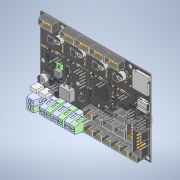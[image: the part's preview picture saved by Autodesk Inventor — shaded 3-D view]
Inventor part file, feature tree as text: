
AUTODESK INVENTOR PART (.ipt)
format: ipt  version: 2022 (Build 260153000, 153)  size: 26,488,320 bytes
history: native  units: in
note: dims shown in document units (in); Inventor stores cm internally (conversion verified against a paired STEP export)
features: other x489, extrude x194, sketch x22, fillet x4
ambient origin geometry x8: Origin, YZ Plane, XZ Plane, XY Plane, X Axis, Y Axis, Z Axis, Center Point
bodies: Solid1 (feature_tree), Solid2 (feature_tree), Solid3 (feature_tree), Solid4 (feature_tree), Solid5 (feature_tree), Solid6 (feature_tree), Solid7 (feature_tree), Solid8 (feature_tree), Solid9 (feature_tree), Solid10 (feature_tree), Solid11 (feature_tree), Solid12 (feature_tree), Solid13 (feature_tree), Solid14 (feature_tree), Solid15 (feature_tree), Solid16 (feature_tree), Solid17 (feature_tree), Solid18 (feature_tree), Solid19 (feature_tree), Solid20 (feature_tree), Solid21 (feature_tree), Solid22 (feature_tree), Solid23 (feature_tree), Solid24 (feature_tree), Solid25 (feature_tree), Solid26 (feature_tree), Solid27 (feature_tree), Solid28 (feature_tree), Solid29 (feature_tree), Solid30 (feature_tree), Solid31 (feature_tree), Solid32 (feature_tree), Solid33 (feature_tree), Solid34 (feature_tree), Solid35 (feature_tree), Solid36 (feature_tree), Solid37 (feature_tree), Solid38 (feature_tree), Solid39 (feature_tree), Solid40 (feature_tree), Solid41 (feature_tree), Solid42 (feature_tree), Solid43 (feature_tree), Solid44 (feature_tree), Solid45 (feature_tree), Solid46 (feature_tree), Solid47 (feature_tree), Solid48 (feature_tree), Solid49 (feature_tree), Solid50 (feature_tree), Solid51 (feature_tree), Solid52 (feature_tree), Solid53 (feature_tree), Solid54 (feature_tree), Solid55 (feature_tree), Solid56 (feature_tree), Solid57 (feature_tree), Solid58 (feature_tree), Solid59 (feature_tree), Solid60 (feature_tree), Solid61 (feature_tree), Solid62 (feature_tree), Solid63 (feature_tree), Solid64 (feature_tree), Solid65 (feature_tree), Solid66 (feature_tree), Solid67 (feature_tree), Solid68 (feature_tree), Solid69 (feature_tree), Solid70 (feature_tree), Solid71 (feature_tree), Solid72 (feature_tree), Solid73 (feature_tree), Solid74 (feature_tree), Solid75 (feature_tree), Solid76 (feature_tree), Solid77 (feature_tree), Solid78 (feature_tree), Solid79 (feature_tree), Solid80 (feature_tree), Solid81 (feature_tree), Solid82 (feature_tree), Solid83 (feature_tree), Solid84 (feature_tree), Solid85 (feature_tree), Solid86 (feature_tree), Solid87 (feature_tree), Solid88 (feature_tree), Solid89 (feature_tree), Solid90 (feature_tree), Solid91 (feature_tree), Solid92 (feature_tree), Solid93 (feature_tree), Solid94 (feature_tree), Solid95 (feature_tree), Solid96 (feature_tree), Solid97 (feature_tree), Solid98 (feature_tree), Solid99 (feature_tree), Solid100 (feature_tree), Solid101 (feature_tree), Solid102 (feature_tree), Solid103 (feature_tree), Solid104 (feature_tree), Solid105 (feature_tree), Solid106 (feature_tree), Solid107 (feature_tree), Solid108 (feature_tree), Solid109 (feature_tree), Solid110 (feature_tree), Solid111 (feature_tree), Solid112 (feature_tree), Solid113 (feature_tree), Solid114 (feature_tree), Solid115 (feature_tree), Solid116 (feature_tree), Solid117 (feature_tree), Solid118 (feature_tree), Solid119 (feature_tree), Solid120 (feature_tree), Solid121 (feature_tree), Solid122 (feature_tree), Solid123 (feature_tree), Solid124 (feature_tree), Solid125 (feature_tree), Solid126 (feature_tree), Solid127 (feature_tree), Solid128 (feature_tree), Solid129 (feature_tree), Solid130 (feature_tree), Solid131 (feature_tree), Solid132 (feature_tree), Solid133 (feature_tree), Solid134 (feature_tree), Solid135 (feature_tree), Solid136 (feature_tree), Solid137 (feature_tree), Solid138 (feature_tree), Solid139 (feature_tree), Solid140 (feature_tree), Solid141 (feature_tree), Solid142 (feature_tree), Solid143 (feature_tree), Solid144 (feature_tree), Solid145 (feature_tree), Solid146 (feature_tree), Solid147 (feature_tree), Solid148 (feature_tree), Solid149 (feature_tree), Solid150 (feature_tree), Solid151 (feature_tree), Solid152 (feature_tree), Solid153 (feature_tree), Solid154 (feature_tree), Solid155 (feature_tree), Solid156 (feature_tree), Solid157 (feature_tree), Solid158 (feature_tree), Solid159 (feature_tree), Solid160 (feature_tree), Solid161 (feature_tree), Solid162 (feature_tree), Solid163 (feature_tree), Solid164 (feature_tree), Solid165 (feature_tree), Solid166 (feature_tree), Solid167 (feature_tree), Solid168 (feature_tree), Solid169 (feature_tree), Solid170 (feature_tree), Solid171 (feature_tree), Solid172 (feature_tree), Solid173 (feature_tree), Solid174 (feature_tree), Solid175 (feature_tree), Solid176 (feature_tree), Solid177 (feature_tree), Solid178 (feature_tree), Solid179 (feature_tree), Solid180 (feature_tree), Solid181 (feature_tree), Solid182 (feature_tree), Solid183 (feature_tree), Solid184 (feature_tree), Solid185 (feature_tree), Solid186 (feature_tree), Solid187 (feature_tree), Solid188 (feature_tree), Solid189 (feature_tree), Solid190 (feature_tree), Solid191 (feature_tree), Solid192 (feature_tree), Solid193 (feature_tree), Solid194 (feature_tree), Solid195 (feature_tree), Solid196 (feature_tree), Solid197 (feature_tree), Solid198 (feature_tree), Solid199 (feature_tree), Solid200 (feature_tree), Solid201 (feature_tree), Solid202 (feature_tree), Solid203 (feature_tree), Solid204 (feature_tree), Solid205 (feature_tree), Solid206 (feature_tree), Solid207 (feature_tree), Solid208 (feature_tree), Solid209 (feature_tree), Solid210 (feature_tree), Solid211 (feature_tree), Solid212 (feature_tree), Solid213 (feature_tree), Solid214 (feature_tree), Solid215 (feature_tree), Solid216 (feature_tree), Solid217 (feature_tree), Solid218 (feature_tree), Solid219 (feature_tree), Solid220 (feature_tree), Solid221 (feature_tree), Solid222 (feature_tree), Solid223 (feature_tree), Solid224 (feature_tree), Solid225 (feature_tree), Solid226 (feature_tree), Solid227 (feature_tree), Solid228 (feature_tree), Solid229 (feature_tree), Solid230 (feature_tree), Solid231 (feature_tree), Solid232 (feature_tree), Solid233 (feature_tree), Solid234 (feature_tree), Solid235 (feature_tree), Solid236 (feature_tree), Solid237 (feature_tree), Solid238 (feature_tree), Solid239 (feature_tree), Solid240 (feature_tree), Solid241 (feature_tree), Solid242 (feature_tree), Solid243 (feature_tree), Solid244 (feature_tree), Solid245 (feature_tree), Solid246 (feature_tree), Solid247 (feature_tree), Solid248 (feature_tree), Solid249 (feature_tree), Solid250 (feature_tree), Solid251 (feature_tree), Solid252 (feature_tree), Solid253 (feature_tree), Solid254 (feature_tree), Solid255 (feature_tree), Solid256 (feature_tree), Solid257 (feature_tree), Solid258 (feature_tree), Solid259 (feature_tree), Solid260 (feature_tree), Solid261 (feature_tree), Solid262 (feature_tree), Solid263 (feature_tree), Solid264 (feature_tree), Solid265 (feature_tree), Solid266 (feature_tree), Solid267 (feature_tree), Solid268 (feature_tree), Solid269 (feature_tree), Solid270 (feature_tree), Solid271 (feature_tree), Solid272 (feature_tree), Solid273 (feature_tree), Solid274 (feature_tree), Solid275 (feature_tree), Solid276 (feature_tree), Solid277 (feature_tree), Solid278 (feature_tree), Solid279 (feature_tree), Solid280 (feature_tree), Solid281 (feature_tree), Solid282 (feature_tree), Solid283 (feature_tree), Solid284 (feature_tree), Solid285 (feature_tree), Solid286 (feature_tree), Solid287 (feature_tree), Solid288 (feature_tree), Solid289 (feature_tree), Solid290 (feature_tree), Solid291 (feature_tree), Solid292 (feature_tree), Solid293 (feature_tree), Solid294 (feature_tree), Solid295 (feature_tree), Solid296 (feature_tree), Solid297 (feature_tree), Solid298 (feature_tree), Solid299 (feature_tree), Solid300 (feature_tree), Solid301 (feature_tree), Solid302 (feature_tree), Solid303 (feature_tree), Solid304 (feature_tree), Solid305 (feature_tree), Solid306 (feature_tree), Solid307 (feature_tree), Solid308 (feature_tree), Solid309 (feature_tree), Solid310 (feature_tree), Solid311 (feature_tree), Solid312 (feature_tree), Solid313 (feature_tree), Solid314 (feature_tree), Solid315 (feature_tree), Solid316 (feature_tree), Solid317 (feature_tree), Solid318 (feature_tree), Solid319 (feature_tree), Solid320 (feature_tree), Solid321 (feature_tree), Solid322 (feature_tree), Solid323 (feature_tree), Solid324 (feature_tree), Solid325 (feature_tree), Solid326 (feature_tree), Solid327 (feature_tree), Solid328 (feature_tree), Solid329 (feature_tree), Solid330 (feature_tree), Solid331 (feature_tree), Solid332 (feature_tree), Solid333 (feature_tree), Solid334 (feature_tree), Solid335 (feature_tree), Solid336 (feature_tree), Solid337 (feature_tree), Solid338 (feature_tree), Solid339 (feature_tree), Solid340 (feature_tree), Solid341 (feature_tree), Solid342 (feature_tree), Solid343 (feature_tree), Solid344 (feature_tree), Solid345 (feature_tree), Solid346 (feature_tree), Solid347 (feature_tree), Solid348 (feature_tree), Solid349 (feature_tree), Solid350 (feature_tree), Solid351 (feature_tree), Solid352 (feature_tree), Solid353 (feature_tree), Solid354 (feature_tree), Solid355 (feature_tree), Solid356 (feature_tree), Solid357 (feature_tree), Solid358 (feature_tree), Solid359 (feature_tree), Solid360 (feature_tree), Solid361 (feature_tree), Solid362 (feature_tree), Solid363 (feature_tree), Solid364 (feature_tree), Solid365 (feature_tree), Solid366 (feature_tree), Solid367 (feature_tree), Solid368 (feature_tree), Solid369 (feature_tree), Solid370 (feature_tree), Solid371 (feature_tree), Solid372 (feature_tree), Solid373 (feature_tree), Solid374 (feature_tree), Solid375 (feature_tree), Solid376 (feature_tree), Solid377 (feature_tree), Solid378 (feature_tree), Solid379 (feature_tree), Solid380 (feature_tree), Solid381 (feature_tree), Solid382 (feature_tree), Solid383 (feature_tree), Solid384 (feature_tree), Solid385 (feature_tree), Solid386 (feature_tree), Solid387 (feature_tree), Solid388 (feature_tree), Solid389 (feature_tree), Solid390 (feature_tree), Solid391 (feature_tree), Solid392 (feature_tree), Solid393 (feature_tree), Solid394 (feature_tree), Solid395 (feature_tree), Solid396 (feature_tree), Solid397 (feature_tree), Solid398 (feature_tree), Solid399 (feature_tree), Solid400 (feature_tree), Solid401 (feature_tree), Solid402 (feature_tree), Solid403 (feature_tree), Solid404 (feature_tree), Solid405 (feature_tree), Solid406 (feature_tree), Solid407 (feature_tree), Solid408 (feature_tree), Solid409 (feature_tree), Solid410 (feature_tree), Solid411 (feature_tree), Solid412 (feature_tree), Solid413 (feature_tree), Solid414 (feature_tree), Solid415 (feature_tree), Solid416 (feature_tree), Solid417 (feature_tree), Solid418 (feature_tree), Solid419 (feature_tree), Solid420 (feature_tree), Solid421 (feature_tree), Solid422 (feature_tree), Solid423 (feature_tree), Solid424 (feature_tree), Solid425 (feature_tree), Solid426 (feature_tree), Solid427 (feature_tree), Solid428 (feature_tree), Solid429 (feature_tree), Solid430 (feature_tree), Solid431 (feature_tree), Solid432 (feature_tree), Solid433 (feature_tree), Solid434 (feature_tree), Solid435 (feature_tree), Solid436 (feature_tree), Solid437 (feature_tree), Solid438 (feature_tree), Solid439 (feature_tree), Solid440 (feature_tree), Solid441 (feature_tree), Solid442 (feature_tree), Solid443 (feature_tree), Solid444 (feature_tree), Solid445 (feature_tree), Solid446 (feature_tree), Solid447 (feature_tree), Solid448 (feature_tree), Solid449 (feature_tree), Solid450 (feature_tree), Solid451 (feature_tree), Solid452 (feature_tree), Solid453 (feature_tree), Solid454 (feature_tree), Solid455 (feature_tree), Solid456 (feature_tree), Solid457 (feature_tree), Solid458 (feature_tree), Solid459 (feature_tree), Solid460 (feature_tree), Solid461 (feature_tree), Solid462 (feature_tree), Solid463 (feature_tree), Solid464 (feature_tree), Solid465 (feature_tree), Solid466 (feature_tree), Solid467 (feature_tree), Solid468 (feature_tree), Solid469 (feature_tree), Solid470 (feature_tree), Solid471 (feature_tree), Solid472 (feature_tree), Solid473 (feature_tree), Solid474 (feature_tree), Solid475 (feature_tree), Solid476 (feature_tree), Solid477 (feature_tree), Solid478 (feature_tree), Solid479 (feature_tree), Solid480 (feature_tree), Solid481 (feature_tree), Solid482 (feature_tree), Solid483 (feature_tree), Solid484 (feature_tree), Solid485 (feature_tree), Solid486 (feature_tree), Solid487 (feature_tree), Solid488 (feature_tree), Solid489 (feature_tree), Solid490 (feature_tree), Solid491 (feature_tree), Solid492 (feature_tree), Solid493 (feature_tree), Solid494 (feature_tree), Solid495 (feature_tree), Solid496 (feature_tree), Solid497 (feature_tree), Solid498 (feature_tree), Solid499 (feature_tree), Solid500 (feature_tree), Solid501 (feature_tree), Solid502 (feature_tree), Solid503 (feature_tree), Solid504 (feature_tree), Solid505 (feature_tree), Solid506 (feature_tree), Solid507 (feature_tree), Solid508 (feature_tree), Solid509 (feature_tree), Solid510 (feature_tree), Solid511 (feature_tree), Solid512 (feature_tree), Solid513 (feature_tree), Solid514 (feature_tree), Solid515 (feature_tree), Solid516 (feature_tree), Solid517 (feature_tree), Solid518 (feature_tree), Solid519 (feature_tree), Solid520 (feature_tree), Solid521 (feature_tree), Solid522 (feature_tree), Solid523 (feature_tree), Solid524 (feature_tree), Solid525 (feature_tree), Solid526 (feature_tree), Solid527 (feature_tree), Solid528 (feature_tree), Solid529 (feature_tree), Solid530 (feature_tree), Solid531 (feature_tree), Solid532 (feature_tree), Solid533 (feature_tree), Solid534 (feature_tree), Solid535 (feature_tree), Solid536 (feature_tree), Solid537 (feature_tree), Solid538 (feature_tree), Solid539 (feature_tree), Solid540 (feature_tree), Solid541 (feature_tree), Solid542 (feature_tree), Solid543 (feature_tree), Solid544 (feature_tree), Solid545 (feature_tree), Solid546 (feature_tree), Solid547 (feature_tree), Solid548 (feature_tree), Solid549 (feature_tree), Solid550 (feature_tree), Solid551 (feature_tree), Solid552 (feature_tree), Solid553 (feature_tree), Solid554 (feature_tree), Solid555 (feature_tree), Solid556 (feature_tree), Solid557 (feature_tree), Solid558 (feature_tree), Solid559 (feature_tree), Solid560 (feature_tree), Solid561 (feature_tree), Solid562 (feature_tree), Solid563 (feature_tree), Solid564 (feature_tree), Solid565 (feature_tree), Solid566 (feature_tree), Solid567 (feature_tree), Solid568 (feature_tree), Solid569 (feature_tree), Solid570 (feature_tree), Solid571 (feature_tree), Solid572 (feature_tree), Solid573 (feature_tree), Solid574 (feature_tree), Solid575 (feature_tree), Solid576 (feature_tree), Solid577 (feature_tree), Solid578 (feature_tree), Solid579 (feature_tree), Solid580 (feature_tree), Solid581 (feature_tree), Solid582 (feature_tree), Solid583 (feature_tree), Solid584 (feature_tree), Solid585 (feature_tree), Solid586 (feature_tree), Solid587 (feature_tree), Solid588 (feature_tree), Solid589 (feature_tree), Solid590 (feature_tree), Solid591 (feature_tree), Solid592 (feature_tree), Solid593 (feature_tree), Solid594 (feature_tree), Solid595 (feature_tree), Solid596 (feature_tree), Solid597 (feature_tree), Solid598 (feature_tree), Solid599 (feature_tree), Solid600 (feature_tree), Solid601 (feature_tree), Solid602 (feature_tree), Solid603 (feature_tree), Solid604 (feature_tree), Solid605 (feature_tree), Solid606 (feature_tree), Solid607 (feature_tree), Solid608 (feature_tree), Solid609 (feature_tree), Solid610 (feature_tree), Solid611 (feature_tree), Solid612 (feature_tree), Solid613 (feature_tree), Solid614 (feature_tree), Solid615 (feature_tree), Solid616 (feature_tree), Solid617 (feature_tree), Solid618 (feature_tree), Solid619 (feature_tree), Solid620 (feature_tree), Solid621 (feature_tree), Solid622 (feature_tree), Solid623 (feature_tree), Solid624 (feature_tree), Solid625 (feature_tree), Solid626 (feature_tree), Solid627 (feature_tree), Solid628 (feature_tree), Solid629 (feature_tree), Solid630 (feature_tree), Solid631 (feature_tree), Solid632 (feature_tree), Solid633 (feature_tree), Solid634 (feature_tree), Solid635 (feature_tree), Solid636 (feature_tree), Solid637 (feature_tree), Solid638 (feature_tree), Solid639 (feature_tree), Solid640 (feature_tree), Solid641 (feature_tree), Solid642 (feature_tree), Solid643 (feature_tree), Solid644 (feature_tree), Solid645 (feature_tree), Solid646 (feature_tree), Solid647 (feature_tree), Solid648 (feature_tree), Solid649 (feature_tree), Solid650 (feature_tree), Solid651 (feature_tree), Solid652 (feature_tree), Solid653 (feature_tree), Solid654 (feature_tree), Solid655 (feature_tree), Solid656 (feature_tree), Solid657 (feature_tree), Solid658 (feature_tree), Solid659 (feature_tree), Solid660 (feature_tree), Solid661 (feature_tree), Solid662 (feature_tree), Solid663 (feature_tree), Solid664 (feature_tree), Solid665 (feature_tree), Solid666 (feature_tree), Solid667 (feature_tree), Solid668 (feature_tree), Solid669 (feature_tree), Solid670 (feature_tree), Solid671 (feature_tree), Solid672 (feature_tree), Solid673 (feature_tree), Solid674 (feature_tree), Solid675 (feature_tree), Solid676 (feature_tree), Solid677 (feature_tree), Solid678 (feature_tree), Solid679 (feature_tree), Solid680 (feature_tree), Solid681 (feature_tree), Solid682 (feature_tree), Solid683 (feature_tree), Solid684 (feature_tree), Solid685 (feature_tree), Solid686 (feature_tree), Solid687 (feature_tree), Solid688 (feature_tree), Solid689 (feature_tree), Solid690 (feature_tree), Solid691 (feature_tree), Solid692 (feature_tree), Solid693 (feature_tree), Solid694 (feature_tree), Solid695 (feature_tree), Solid696 (feature_tree), Solid697 (feature_tree), Solid698 (feature_tree), Solid699 (feature_tree), Solid700 (feature_tree), Solid701 (feature_tree), Solid702 (feature_tree), Solid703 (feature_tree), Solid704 (feature_tree), Solid705 (feature_tree), Solid706 (feature_tree), Solid707 (feature_tree), Solid708 (feature_tree), Solid709 (feature_tree), Solid710 (feature_tree), Solid711 (feature_tree), Solid712 (feature_tree), Solid713 (feature_tree), Solid714 (feature_tree), Solid715 (feature_tree), Solid716 (feature_tree), Solid717 (feature_tree), Solid718 (feature_tree), Solid719 (feature_tree), Solid720 (feature_tree), Solid721 (feature_tree), Solid722 (feature_tree), Solid723 (feature_tree), Solid724 (feature_tree), Solid725 (feature_tree), Solid726 (feature_tree), Solid727 (feature_tree), Solid728 (feature_tree), Solid729 (feature_tree), Solid730 (feature_tree), Solid731 (feature_tree), Solid732 (feature_tree), Solid733 (feature_tree), Solid734 (feature_tree), Solid735 (feature_tree), Solid736 (feature_tree), Solid737 (feature_tree), Solid738 (feature_tree), Solid739 (feature_tree), Solid740 (feature_tree), Solid741 (feature_tree), Solid742 (feature_tree), Solid743 (feature_tree), Solid744 (feature_tree), Solid745 (feature_tree), Solid746 (feature_tree), Solid747 (feature_tree), Solid748 (feature_tree), Solid749 (feature_tree), Solid750 (feature_tree), Solid751 (feature_tree), Solid752 (feature_tree), Solid753 (feature_tree), Solid754 (feature_tree), Solid755 (feature_tree), Solid756 (feature_tree), Solid757 (feature_tree), Solid758 (feature_tree), Solid759 (feature_tree), Solid760 (feature_tree)
feature tree (709):
  sketch  "Sketch1"
  sketch  "Sketch2"
  sketch  "Sketch3"
  sketch  "Sketch4"
  sketch  "Sketch5"
  sketch  "Sketch6"
  sketch  "Sketch7"
  sketch  "Sketch8"
  sketch  "Sketch9"
  sketch  "Sketch10"
  sketch  "Sketch11"
  sketch  "Sketch12"
  sketch  "Sketch13"
  sketch  "Sketch14"
  sketch  "Sketch15"
  sketch  "Sketch16"
  sketch  "Sketch17"
  sketch  "Sketch18"
  sketch  "Sketch19"
  sketch  "Sketch20"
  sketch  "Sketch21"
  sketch  "Sketch22"
  other  "Board_1:1"
  other  "KF128_1:1"
  other  "KF128_1:2"
  other  "KF128_1:3"
  other  "KF128_1:4"
  other  "KF128_1:5"
  other  "KF128_1:6"
  other  "KF128_1:7"
  other  "KF128_1:8"
  extrude  "Extruded_1:1"  [1 undecoded]
  extrude  "Extruded (1)_1:1"  [1 undecoded]
  extrude  "Extruded (1)_1:2"  [1 undecoded]
  extrude  "Extruded_1:2"  [1 undecoded]
  extrude  "Extruded (1)_1:3"  [1 undecoded]
  extrude  "Extruded (1)_1:4"  [1 undecoded]
  extrude  "Extruded (2)_1:1"  [1 undecoded]
  extrude  "Extruded (3)_1:1"  [1 undecoded]
  extrude  "Extruded (3)_1:2"  [1 undecoded]
  other  "KF128_2:1"
  other  "KF128_2:2"
  other  "KF128_2:3"
  other  "KF128_2:4"
  other  "KF128_2:5"
  other  "KF128_2:6"
  other  "KF128_2:7"
  other  "KF128_2:8"
  extrude  "Extruded (4)_1:1"  [1 undecoded]
  extrude  "Extruded (5)_1:1"  [1 undecoded]
  extrude  "Extruded (6)_1:1"  [1 undecoded]
  extrude  "Extruded (7)_1:1"  [1 undecoded]
  extrude  "Extruded (8)_1:1"  [1 undecoded]
  other  "Cylinder_1:1"
  other  "Cylinder_1:2"
  other  "Cylinder_1:3"
  other  "Cylinder_1:4"
  extrude  "Extruded (9)_1:1"  [1 undecoded]
  other  "usb_b-c_1:1"
  other  "usb_b-c_1:2"
  other  "usb_b-c_1:3"
  other  "usb_b-c_1:4"
  other  "usb_b-c_1:5"
  other  "usb_b-c_1:6"
  other  "User_Library-XH2_54_2PIN_RGB0_1:1"
  other  "User_Library-XH2_54_2PIN_RGB0_1:2"
  other  "User_Library-XH2_54_2PIN_RGB0_1:3"
  other  "User_Library-XH2_54_2PIN_RGB0_1:4"
  other  "User_Library-XH2_54_2PIN_RGB0_1:5"
  other  "User_Library-XH2_54_2PIN_RGB0_2:1"
  other  "User_Library-XH2_54_2PIN_RGB0_2:2"
  other  "User_Library-XH2_54_2PIN_RGB0_2:3"
  other  "User_Library-XH2_54_2PIN_RGB0_2:4"
  other  "User_Library-XH2_54_2PIN_RGB0_2:5"
  other  "Fusion_1:1"
  other  "Fusion_1:2"
  other  "Fusion_1:3"
  other  "Fusion_1:4"
  other  "Fusion_1:5"
  other  "Fusion_1:6"
  other  "Fusion_1:7"
  other  "Fusion_1:8"
  other  "Fusion_1:9"
  other  "Fusion_1:10"
  other  "Fusion_1:11"
  other  "Fusion_1:12"
  other  "Fusion_1:13"
  other  "Fusion_1:14"
  other  "Fusion_1:15"
  other  "Fusion_1:16"
  other  "Fusion_1:17"
  other  "Fusion_1:18"
  other  "Fusion_1:19"
  other  "Fusion_1:20"
  other  "Fusion_1:21"
  other  "Fusion_1:22"
  other  "Fusion_1:23"
  other  "Fusion_1:24"
  other  "Fusion_1:25"
  other  "Fusion_1:26"
  other  "Fusion_1:27"
  other  "Fusion_1:28"
  other  "Fusion_1:29"
  fillet  "Fillet_1:1"  [1 undecoded]
  other  "Fusion_1:30"
  other  "Fusion_1:31"
  other  "Fusion_1:32"
  other  "Fusion_1:33"
  other  "Fusion_1:34"
  other  "Fusion_1:35"
  other  "Fusion_1:36"
  other  "Fusion_1:37"
  other  "Fusion_1:38"
  other  "Fusion_1:39"
  other  "Fusion_1:40"
  other  "Fusion_1:41"
  other  "Fusion_1:42"
  other  "Fusion_1:43"
  other  "Fusion_1:44"
  other  "Fusion_1:45"
  other  "Fusion_1:46"
  other  "Fusion_1:47"
  other  "Fusion_1:48"
  other  "Fusion_1:49"
  other  "Fusion_1:50"
  other  "Fusion_1:51"
  other  "Fusion_1:52"
  other  "Fusion_1:53"
  other  "Fusion_1:54"
  other  "Fusion_1:55"
  other  "Fusion_1:56"
  other  "Fusion_1:57"
  other  "Fusion_1:58"
  fillet  "Fillet_1:2"  [1 undecoded]
  other  "Fusion_1:59"
  other  "Fusion_1:60"
  other  "Fusion_1:61"
  other  "Fusion_1:62"
  other  "Fusion_1:63"
  other  "Fusion_1:64"
  other  "Fusion_1:65"
  other  "Fusion_1:66"
  other  "Fusion_1:67"
  other  "Fusion_1:68"
  other  "Fusion_1:69"
  other  "Fusion_1:70"
  other  "Fusion_1:71"
  other  "Fusion_1:72"
  other  "Fusion_1:73"
  other  "Fusion_1:74"
  other  "Fusion_1:75"
  other  "Fusion_1:76"
  other  "Fusion_1:77"
  other  "Fusion_1:78"
  other  "Fusion_1:79"
  other  "Fusion_1:80"
  other  "Fusion_1:81"
  other  "Fusion_1:82"
  other  "Fusion_1:83"
  other  "Fusion_1:84"
  other  "Fusion_1:85"
  other  "Fusion_1:86"
  other  "Fusion_1:87"
  fillet  "Fillet_1:3"  [1 undecoded]
  other  "Fusion_1:88"
  other  "Fusion_1:89"
  other  "Fusion_1:90"
  other  "Fusion_1:91"
  other  "Fusion_1:92"
  other  "Fusion_1:93"
  other  "Fusion_1:94"
  other  "Fusion_1:95"
  other  "Fusion_1:96"
  other  "Fusion_1:97"
  other  "Fusion_1:98"
  other  "Fusion_1:99"
  other  "Fusion_1:100"
  other  "Fusion_1:101"
  other  "Fusion_1:102"
  other  "Fusion_1:103"
  other  "Fusion_1:104"
  other  "Fusion_1:105"
  other  "Fusion_1:106"
  other  "Fusion_1:107"
  other  "Fusion_1:108"
  other  "Fusion_1:109"
  other  "Fusion_1:110"
  other  "Fusion_1:111"
  other  "Fusion_1:112"
  other  "Fusion_1:113"
  other  "Fusion_1:114"
  other  "Fusion_1:115"
  other  "Fusion_1:116"
  fillet  "Fillet_1:4"  [1 undecoded]
  other  "Cylinder (1)_1:1"
  other  "Cylinder (1)_1:2"
  other  "Cylinder (1)_1:3"
  extrude  "Extruded (6)_1:2"  [1 undecoded]
  extrude  "Extruded (10)_1:1"  [1 undecoded]
  extrude  "Extruded (11)_1:1"  [1 undecoded]
  extrude  "Extruded (12)_1:1"  [1 undecoded]
  extrude  "Extruded (5)_1:2"  [1 undecoded]
  other  "User_Library-XH2_54_2PIN_RGB0_3:1"
  other  "User_Library-XH2_54_2PIN_RGB0_3:2"
  other  "User_Library-XH2_54_2PIN_RGB0_3:3"
  other  "User_Library-XH2_54_2PIN_RGB0_3:4"
  other  "User_Library-XH2_54_2PIN_RGB0_3:5"
  other  "User_Library-XH2_54_2PIN_RGB0_4:1"
  other  "User_Library-XH2_54_2PIN_RGB0_4:2"
  other  "User_Library-XH2_54_2PIN_RGB0_4:3"
  other  "User_Library-XH2_54_2PIN_RGB0_4:4"
  other  "User_Library-XH2_54_2PIN_RGB0_4:5"
  other  "User_Library-XH2_54_2PIN_RGB0_5:1"
  other  "User_Library-XH2_54_2PIN_RGB0_5:2"
  other  "User_Library-XH2_54_2PIN_RGB0_5:3"
  other  "User_Library-XH2_54_2PIN_RGB0_5:4"
  other  "User_Library-XH2_54_2PIN_RGB0_5:5"
  extrude  "Extruded (13)_1:1"  [1 undecoded]
  other  "User_Library-XH2_54_2PIN_RGB0_6:1"
  other  "User_Library-XH2_54_2PIN_RGB0_6:2"
  other  "User_Library-XH2_54_2PIN_RGB0_6:3"
  other  "User_Library-XH2_54_2PIN_RGB0_6:4"
  other  "User_Library-XH2_54_2PIN_RGB0_6:5"
  other  "Cylinder (1)_1:4"
  other  "Cylinder (1)_1:5"
  other  "Cylinder (1)_1:6"
  extrude  "Extruded (6)_1:3"  [1 undecoded]
  extrude  "Extruded (10)_1:2"  [1 undecoded]
  extrude  "Extruded (11)_1:2"  [1 undecoded]
  extrude  "Extruded (12)_1:2"  [1 undecoded]
  extrude  "Extruded (5)_1:3"  [1 undecoded]
  other  "User_Library-led_0805_1:1"
  extrude  "Extruded_1:3"  [1 undecoded]
  extrude  "Extruded (1)_1:5"  [1 undecoded]
  extrude  "Extruded (1)_1:6"  [1 undecoded]
  other  "TQFP-64_10x10_1:1"
  other  "User_Library-XH2_54_2PIN_RGB0_7:1"
  other  "User_Library-XH2_54_2PIN_RGB0_7:2"
  other  "User_Library-XH2_54_2PIN_RGB0_7:3"
  other  "User_Library-XH2_54_2PIN_RGB0_7:4"
  other  "User_Library-XH2_54_2PIN_RGB0_7:5"
  extrude  "Extruded (4)_1:2"  [1 undecoded]
  extrude  "Extruded (5)_1:4"  [1 undecoded]
  extrude  "Extruded (6)_1:4"  [1 undecoded]
  extrude  "Extruded (7)_1:2"  [1 undecoded]
  extrude  "Extruded (8)_1:2"  [1 undecoded]
  other  "Cylinder_1:5"
  other  "Cylinder_1:6"
  other  "Cylinder_1:7"
  other  "Cylinder_1:8"
  other  "R0603_1:1"
  other  "R0603_1:2"
  other  "R0603_2:1"
  other  "R0603_2:2"
  other  "R0603_3:1"
  other  "R0603_3:2"
  other  "R0603_4:1"
  other  "R0603_4:2"
  other  "R0603_5:1"
  other  "R0603_5:2"
  other  "R0603_6:1"
  other  "R0603_6:2"
  other  "R0603_7:1"
  other  "R0603_7:2"
  other  "R0603_8:1"
  other  "R0603_8:2"
  other  "R0603_9:1"
  other  "R0603_9:2"
  other  "R0603_10:1"
  other  "R0603_10:2"
  other  "R0603_11:1"
  other  "R0603_11:2"
  other  "R0603_12:1"
  other  "R0603_12:2"
  other  "User_Library-LED_0603_G_Pad004_1:1"
  other  "User_Library-LED_0603_G_Fillet_1:1"
  other  "User_Library-LED_0603_G_Pocket001_1:1"
  other  "User_Library-LED_0603_G_Pad_1:1"
  other  "User_Library-LED_0603_G_Pad004_1:2"
  other  "User_Library-LED_0603_G_Fillet_1:2"
  other  "User_Library-LED_0603_G_Pocket001_1:2"
  other  "User_Library-LED_0603_G_Pad_1:2"
  other  "TSSOP-8_1:1"
  other  "TSSOP-8_1:2"
  other  "TSSOP-8_1:3"
  other  "TSSOP-8_1:4"
  other  "TSSOP-8_1:5"
  other  "TSSOP-8_1:6"
  other  "TSSOP-8_1:7"
  other  "TSSOP-8_1:8"
  other  "TSSOP-8_1:9"
  other  "SO-8_1:1"
  other  "SO-8_1:2"
  other  "SO-8_1:3"
  other  "SO-8_1:4"
  other  "SO-8_1:5"
  other  "SO-8_1:6"
  other  "SO-8_1:7"
  other  "SO-8_1:8"
  other  "SO-8_1:9"
  other  "R0603_13:1"
  other  "R0603_13:2"
  other  "R0603_14:1"
  other  "R0603_14:2"
  other  "R0603_15:1"
  other  "R0603_15:2"
  other  "R0603_16:1"
  other  "R0603_16:2"
  other  "R0603_17:1"
  other  "R0603_17:2"
  other  "R0603_18:1"
  other  "R0603_18:2"
  other  "R0603_19:1"
  other  "R0603_19:2"
  other  "R0603_20:1"
  other  "R0603_20:2"
  other  "R0603_21:1"
  other  "R0603_21:2"
  other  "R0603_22:1"
  other  "R0603_22:2"
  other  "R0603_23:1"
  other  "R0603_23:2"
  extrude  "Extruded (14)_1:1"  [1 undecoded]
  extrude  "Extruded (15)_1:1"  [1 undecoded]
  extrude  "Extruded (16)_1:1"  [1 undecoded]
  extrude  "Extruded (17)_1:1"  [1 undecoded]
  other  "Cylinder (2)_1:1"
  other  "Cylinder (2)_1:2"
  other  "Cylinder (2)_1:3"
  other  "Cylinder (2)_1:4"
  extrude  "Extruded (18)_1:1"  [1 undecoded]
  other  "Cylinder (3)_1:1"
  other  "DO214AC-SMA_S1G_1:1"
  extrude  "Extruded (2)_1:2"  [1 undecoded]
  extrude  "Extruded (3)_1:3"  [1 undecoded]
  extrude  "Extruded (3)_1:4"  [1 undecoded]
  other  "User_Library-0805_SMD_Capacitor_1:1"
  extrude  "Extruded (2)_1:3"  [1 undecoded]
  extrude  "Extruded (3)_1:5"  [1 undecoded]
  extrude  "Extruded (3)_1:6"  [1 undecoded]
  extrude  "Extruded_1:4"  [1 undecoded]
  extrude  "Extruded (1)_1:7"  [1 undecoded]
  extrude  "Extruded (1)_1:8"  [1 undecoded]
  other  "R0603_24:1"
  other  "R0603_24:2"
  other  "R0603_25:1"
  other  "R0603_25:2"
  extrude  "Extruded_1:5"  [1 undecoded]
  extrude  "Extruded (1)_1:9"  [1 undecoded]
  extrude  "Extruded (1)_1:10"  [1 undecoded]
  extrude  "Extruded (19)_1:1"  [1 undecoded]
  extrude  "Extruded (20)_1:1"  [1 undecoded]
  extrude  "Extruded (19)_1:2"  [1 undecoded]
  extrude  "Extruded (2)_1:4"  [1 undecoded]
  extrude  "Extruded (3)_1:7"  [1 undecoded]
  extrude  "Extruded (3)_1:8"  [1 undecoded]
  extrude  "Extruded (2)_1:5"  [1 undecoded]
  extrude  "Extruded (3)_1:9"  [1 undecoded]
  extrude  "Extruded (3)_1:10"  [1 undecoded]
  other  "SL-E_1:1"
  extrude  "Extruded (2)_1:6"  [1 undecoded]
  extrude  "Extruded (3)_1:11"  [1 undecoded]
  extrude  "Extruded (3)_1:12"  [1 undecoded]
  extrude  "Extruded (2)_1:7"  [1 undecoded]
  extrude  "Extruded (3)_1:13"  [1 undecoded]
  extrude  "Extruded (3)_1:14"  [1 undecoded]
  extrude  "Extruded (2)_1:8"  [1 undecoded]
  extrude  "Extruded (3)_1:15"  [1 undecoded]
  extrude  "Extruded (3)_1:16"  [1 undecoded]
  extrude  "Extruded (2)_1:9"  [1 undecoded]
  extrude  "Extruded (3)_1:17"  [1 undecoded]
  extrude  "Extruded (3)_1:18"  [1 undecoded]
  extrude  "Extruded_1:6"  [1 undecoded]
  extrude  "Extruded (1)_1:11"  [1 undecoded]
  extrude  "Extruded (1)_1:12"  [1 undecoded]
  extrude  "Extruded_1:7"  [1 undecoded]
  extrude  "Extruded (1)_1:13"  [1 undecoded]
  extrude  "Extruded (1)_1:14"  [1 undecoded]
  other  "User_Library-0805_SMD_Capacitor_2:1"
  extrude  "Extruded_1:8"  [1 undecoded]
  extrude  "Extruded (1)_1:15"  [1 undecoded]
  extrude  "Extruded (1)_1:16"  [1 undecoded]
  extrude  "Extruded (2)_1:10"  [1 undecoded]
  extrude  "Extruded (3)_1:19"  [1 undecoded]
  extrude  "Extruded (3)_1:20"  [1 undecoded]
  extrude  "Extruded_1:9"  [1 undecoded]
  extrude  "Extruded (1)_1:17"  [1 undecoded]
  extrude  "Extruded (1)_1:18"  [1 undecoded]
  extrude  "Extruded (2)_1:11"  [1 undecoded]
  extrude  "Extruded (3)_1:21"  [1 undecoded]
  extrude  "Extruded (3)_1:22"  [1 undecoded]
  other  "SL-E_2:1"
  extrude  "Extruded_1:10"  [1 undecoded]
  extrude  "Extruded (1)_1:19"  [1 undecoded]
  extrude  "Extruded (1)_1:20"  [1 undecoded]
  other  "User_Library-0805_SMD_Capacitor_3:1"
  extrude  "Extruded (2)_1:12"  [1 undecoded]
  extrude  "Extruded (3)_1:23"  [1 undecoded]
  extrude  "Extruded (3)_1:24"  [1 undecoded]
  extrude  "Extruded_1:11"  [1 undecoded]
  extrude  "Extruded (1)_1:21"  [1 undecoded]
  extrude  "Extruded (1)_1:22"  [1 undecoded]
  other  "User_Library-led_0805_2:1"
  other  "User_Library-LED_0603_G_Pad004_1:3"
  other  "User_Library-LED_0603_G_Fillet_1:3"
  other  "User_Library-LED_0603_G_Pocket001_1:3"
  other  "User_Library-LED_0603_G_Pad_1:3"
  other  "User_Library-LED_0603_G_Pad004_1:4"
  other  "User_Library-LED_0603_G_Fillet_1:4"
  other  "User_Library-LED_0603_G_Pocket001_1:4"
  other  "User_Library-LED_0603_G_Pad_1:4"
  other  "User_Library-XH2_54_2PIN_RGB0_8:1"
  other  "User_Library-XH2_54_2PIN_RGB0_8:2"
  other  "User_Library-XH2_54_2PIN_RGB0_8:3"
  other  "User_Library-XH2_54_2PIN_RGB0_8:4"
  other  "User_Library-XH2_54_2PIN_RGB0_8:5"
  other  "KF128_3:1"
  other  "KF128_3:2"
  other  "KF128_3:3"
  other  "KF128_3:4"
  other  "KF128_3:5"
  other  "KF128_3:6"
  other  "KF128_3:7"
  other  "KF128_3:8"
  other  "R0805_1:1"
  other  "R0805_1:2"
  other  "TO-252_1:1"
  other  "R0603_26:1"
  other  "R0603_26:2"
  other  "R0603_27:1"
  other  "R0603_27:2"
  other  "R0603_28:1"
  other  "R0603_28:2"
  other  "R0603_29:1"
  other  "R0603_29:2"
  other  "R0603_30:1"
  other  "R0603_30:2"
  other  "R0603_31:1"
  other  "R0603_31:2"
  other  "R0603_32:1"
  other  "R0603_32:2"
  other  "R0603_33:1"
  other  "R0603_33:2"
  other  "R0603_34:1"
  other  "R0603_34:2"
  other  "R0603_35:1"
  other  "R0603_35:2"
  other  "R0603_36:1"
  other  "R0603_36:2"
  other  "R0603_37:1"
  other  "R0603_37:2"
  other  "R0603_38:1"
  other  "R0603_38:2"
  other  "R0603_39:1"
  other  "R0603_39:2"
  other  "R0603_40:1"
  other  "R0603_40:2"
  other  "R0603_41:1"
  other  "R0603_41:2"
  other  "R0603_42:1"
  other  "R0603_42:2"
  other  "R0603_43:1"
  other  "R0603_43:2"
  other  "R0603_44:1"
  other  "R0603_44:2"
  other  "R0603_45:1"
  other  "R0603_45:2"
  other  "R0603_46:1"
  other  "R0603_46:2"
  other  "R0603_47:1"
  other  "R0603_47:2"
  other  "R0603_48:1"
  other  "R0603_48:2"
  other  "User_Library-R-0603-Array-4-1_1:1"
  other  "User_Library-R-0603-Array-4-1_2:1"
  other  "User_Library-R-0603-Array-4-1_3:1"
  other  "User_Library-R-0603-Array-4-1_4:1"
  other  "SOT-223_MP04A_1:1"
  other  "SOT-223_MP04A_1:2"
  other  "SOT-223_MP04A_1:3"
  other  "SOT-223_MP04A_1:4"
  other  "SOT-223_MP04A_1:5"
  other  "SOT-223_MP04A_1:6"
  other  "DO214AC-SMA_S1G_2:1"
  other  "DO214AC-SMA_S1G_3:1"
  other  "R0603_49:1"
  other  "R0603_49:2"
  other  "User_Library-GeyerElectronics_KX7_1:1"
  other  "User_Library-GeyerElectronics_KX7_1:2"
  other  "User_Library-GeyerElectronics_KX7_1:3"
  other  "User_Library-GeyerElectronics_KX7_1:4"
  extrude  "Extruded (21)_1:1"  [1 undecoded]
  other  "User_Library-LED_0603_G_Pad004_1:5"
  other  "User_Library-LED_0603_G_Fillet_1:5"
  other  "User_Library-LED_0603_G_Pocket001_1:5"
  other  "User_Library-LED_0603_G_Pad_1:5"
  other  "R0603_50:1"
  other  "R0603_50:2"
  other  "R0603_51:1"
  other  "R0603_51:2"
  other  "R0603_52:1"
  other  "R0603_52:2"
  other  "R0603_53:1"
  other  "R0603_53:2"
  extrude  "Extruded (22)_1:1"  [1 undecoded]
  extrude  "Extruded (23)_1:1"  [1 undecoded]
  other  "Cylinder (4)_1:1"
  other  "Cylinder (4)_1:2"
  other  "Cylinder (4)_1:3"
  other  "Cylinder (4)_1:4"
  other  "Cylinder (4)_1:5"
  other  "Cylinder (4)_1:6"
  other  "Cylinder (4)_1:7"
  other  "Cylinder (4)_1:8"
  other  "Cylinder (4)_1:9"
  other  "Cylinder (4)_1:10"
  extrude  "Extruded (2)_1:13"  [1 undecoded]
  extrude  "Extruded (3)_1:25"  [1 undecoded]
  extrude  "Extruded (3)_1:26"  [1 undecoded]
  extrude  "Extruded_1:12"  [1 undecoded]
  extrude  "Extruded (1)_1:23"  [1 undecoded]
  extrude  "Extruded (1)_1:24"  [1 undecoded]
  extrude  "Extruded (2)_1:14"  [1 undecoded]
  extrude  "Extruded (3)_1:27"  [1 undecoded]
  extrude  "Extruded (3)_1:28"  [1 undecoded]
  other  "SL-E_3:1"
  extrude  "Extruded (2)_1:15"  [1 undecoded]
  extrude  "Extruded (3)_1:29"  [1 undecoded]
  extrude  "Extruded (3)_1:30"  [1 undecoded]
  extrude  "Extruded_1:13"  [1 undecoded]
  extrude  "Extruded (1)_1:25"  [1 undecoded]
  extrude  "Extruded (1)_1:26"  [1 undecoded]
  extrude  "Extruded (2)_1:16"  [1 undecoded]
  extrude  "Extruded (3)_1:31"  [1 undecoded]
  extrude  "Extruded (3)_1:32"  [1 undecoded]
  extrude  "Extruded (2)_1:17"  [1 undecoded]
  extrude  "Extruded (3)_1:33"  [1 undecoded]
  extrude  "Extruded (3)_1:34"  [1 undecoded]
  extrude  "Extruded (2)_1:18"  [1 undecoded]
  extrude  "Extruded (3)_1:35"  [1 undecoded]
  extrude  "Extruded (3)_1:36"  [1 undecoded]
  extrude  "Extruded (2)_1:19"  [1 undecoded]
  extrude  "Extruded (3)_1:37"  [1 undecoded]
  extrude  "Extruded (3)_1:38"  [1 undecoded]
  other  "SL-E_4:1"
  extrude  "Extruded (2)_1:20"  [1 undecoded]
  extrude  "Extruded (3)_1:39"  [1 undecoded]
  extrude  "Extruded (3)_1:40"  [1 undecoded]
  extrude  "Extruded_1:14"  [1 undecoded]
  extrude  "Extruded (1)_1:27"  [1 undecoded]
  extrude  "Extruded (1)_1:28"  [1 undecoded]
  extrude  "Extruded_1:15"  [1 undecoded]
  extrude  "Extruded (1)_1:29"  [1 undecoded]
  extrude  "Extruded (1)_1:30"  [1 undecoded]
  extrude  "Extruded (2)_1:21"  [1 undecoded]
  extrude  "Extruded (3)_1:41"  [1 undecoded]
  extrude  "Extruded (3)_1:42"  [1 undecoded]
  extrude  "Extruded_1:16"  [1 undecoded]
  extrude  "Extruded (1)_1:31"  [1 undecoded]
  extrude  "Extruded (1)_1:32"  [1 undecoded]
  other  "User_Library-0805_SMD_Capacitor_4:1"
  extrude  "Extruded (2)_1:22"  [1 undecoded]
  extrude  "Extruded (3)_1:43"  [1 undecoded]
  extrude  "Extruded (3)_1:44"  [1 undecoded]
  other  "SL-E_5:1"
  extrude  "Extruded (2)_1:23"  [1 undecoded]
  extrude  "Extruded (3)_1:45"  [1 undecoded]
  extrude  "Extruded (3)_1:46"  [1 undecoded]
  extrude  "Extruded_1:17"  [1 undecoded]
  extrude  "Extruded (1)_1:33"  [1 undecoded]
  extrude  "Extruded (1)_1:34"  [1 undecoded]
  extrude  "Extruded_1:18"  [1 undecoded]
  extrude  "Extruded (1)_1:35"  [1 undecoded]
  extrude  "Extruded (1)_1:36"  [1 undecoded]
  extrude  "Extruded (2)_1:24"  [1 undecoded]
  extrude  "Extruded (3)_1:47"  [1 undecoded]
  extrude  "Extruded (3)_1:48"  [1 undecoded]
  extrude  "Extruded_1:19"  [1 undecoded]
  extrude  "Extruded (1)_1:37"  [1 undecoded]
  extrude  "Extruded (1)_1:38"  [1 undecoded]
  extrude  "Extruded_1:20"  [1 undecoded]
  extrude  "Extruded (1)_1:39"  [1 undecoded]
  extrude  "Extruded (1)_1:40"  [1 undecoded]
  extrude  "Extruded (4)_1:3"  [1 undecoded]
  extrude  "Extruded (5)_1:5"  [1 undecoded]
  extrude  "Extruded (6)_1:5"  [1 undecoded]
  extrude  "Extruded (7)_1:3"  [1 undecoded]
  extrude  "Extruded (8)_1:3"  [1 undecoded]
  other  "Cylinder_1:9"
  other  "Cylinder_1:10"
  other  "Cylinder_1:11"
  other  "Cylinder_1:12"
  other  "TO263_1:1"
  other  "R0603_54:1"
  other  "R0603_54:2"
  other  "R0805_2:1"
  other  "R0805_2:2"
  other  "R0603_55:1"
  other  "R0603_55:2"
  other  "R0805_3:1"
  other  "R0805_3:2"
  other  "R0603_56:1"
  other  "R0603_56:2"
  other  "R0603_57:1"
  other  "R0603_57:2"
  other  "R0805_4:1"
  other  "R0805_4:2"
  other  "R0603_58:1"
  other  "R0603_58:2"
  other  "R0805_5:1"
  other  "R0805_5:2"
  other  "R0603_59:1"
  other  "R0603_59:2"
  other  "R0603_60:1"
  other  "R0603_60:2"
  other  "R0603_61:1"
  other  "R0603_61:2"
  other  "R0603_62:1"
  other  "R0603_62:2"
  other  "R0805_6:1"
  other  "R0805_6:2"
  other  "R0603_63:1"
  other  "R0603_63:2"
  other  "R0805_7:1"
  other  "R0805_7:2"
  other  "R0603_64:1"
  other  "R0603_64:2"
  other  "R0603_65:1"
  other  "R0603_65:2"
  other  "R0603_66:1"
  other  "R0603_66:2"
  other  "R0603_67:1"
  other  "R0603_67:2"
  other  "R0603_68:1"
  other  "R0603_68:2"
  other  "R0603_69:1"
  other  "R0603_69:2"
  other  "R0603_70:1"
  other  "R0603_70:2"
  other  "R0805_8:1"
  other  "R0805_8:2"
  other  "R0603_71:1"
  other  "R0603_71:2"
  other  "R0805_9:1"
  other  "R0805_9:2"
  other  "R0603_72:1"
  other  "R0603_72:2"
  other  "TSSOP14-1_1:1"
  other  "TSSOP14-1_1:2"
  other  "TSSOP14-1_1:3"
  other  "TSSOP14-1_1:4"
  other  "TSSOP14-1_1:5"
  other  "TSSOP14-1_1:6"
  other  "TSSOP14-1_1:7"
  other  "TSSOP14-1_1:8"
  other  "SOT-23-5_1:1"
  other  "SOT-23-5_1:2"
  other  "SOT-23-5_1:3"
  other  "SOT-23-5_1:4"
  other  "SOT-23-5_1:5"
  other  "SOT-23-5_1:6"
  other  "SOT-23-5_1:7"
  extrude  "Extruded (4)_1:4"  [1 undecoded]
  extrude  "Extruded (5)_1:6"  [1 undecoded]
  extrude  "Extruded (6)_1:6"  [1 undecoded]
  extrude  "Extruded (7)_1:4"  [1 undecoded]
  extrude  "Extruded (8)_1:4"  [1 undecoded]
  other  "Cylinder_1:13"
  other  "Cylinder_1:14"
  other  "Cylinder_1:15"
  other  "Cylinder_1:16"
  extrude  "Extruded (4)_1:5"  [1 undecoded]
  extrude  "Extruded (5)_1:7"  [1 undecoded]
  extrude  "Extruded (6)_1:7"  [1 undecoded]
  extrude  "Extruded (7)_1:5"  [1 undecoded]
  extrude  "Extruded (8)_1:5"  [1 undecoded]
  other  "Cylinder_1:17"
  other  "Cylinder_1:18"
  other  "Cylinder_1:19"
  other  "Cylinder_1:20"
  other  "KF128_4:1"
  other  "KF128_4:2"
  other  "KF128_4:3"
  other  "KF128_4:4"
  other  "KF128_4:5"
  other  "KF128_4:6"
  other  "KF128_4:7"
  other  "KF128_4:8"
  other  "DO214AC-SMA_S1G_4:1"
  other  "Fuse_1812_1:1"
  other  "Cylinder (1)_1:7"
  other  "Cylinder (1)_1:8"
  other  "Cylinder (1)_1:9"
  extrude  "Extruded (6)_1:8"  [1 undecoded]
  extrude  "Extruded (10)_1:3"  [1 undecoded]
  extrude  "Extruded (11)_1:3"  [1 undecoded]
  extrude  "Extruded (12)_1:3"  [1 undecoded]
  extrude  "Extruded (5)_1:8"  [1 undecoded]
  extrude  "Extruded_1:21"  [1 undecoded]
  extrude  "Extruded (1)_1:41"  [1 undecoded]
  extrude  "Extruded (1)_1:42"  [1 undecoded]
  extrude  "Extruded_1:22"  [1 undecoded]
  extrude  "Extruded (1)_1:43"  [1 undecoded]
  extrude  "Extruded (1)_1:44"  [1 undecoded]
  extrude  "Extruded_1:23"  [1 undecoded]
  extrude  "Extruded (1)_1:45"  [1 undecoded]
  extrude  "Extruded (1)_1:46"  [1 undecoded]
  other  "Composite1"
  other  "Srf1"
note: 198 required parameter values undecoded (feature->parameter linkage not recoverable at this tier; creation-order binding heuristic only, values carry confidence <= 0.55)
